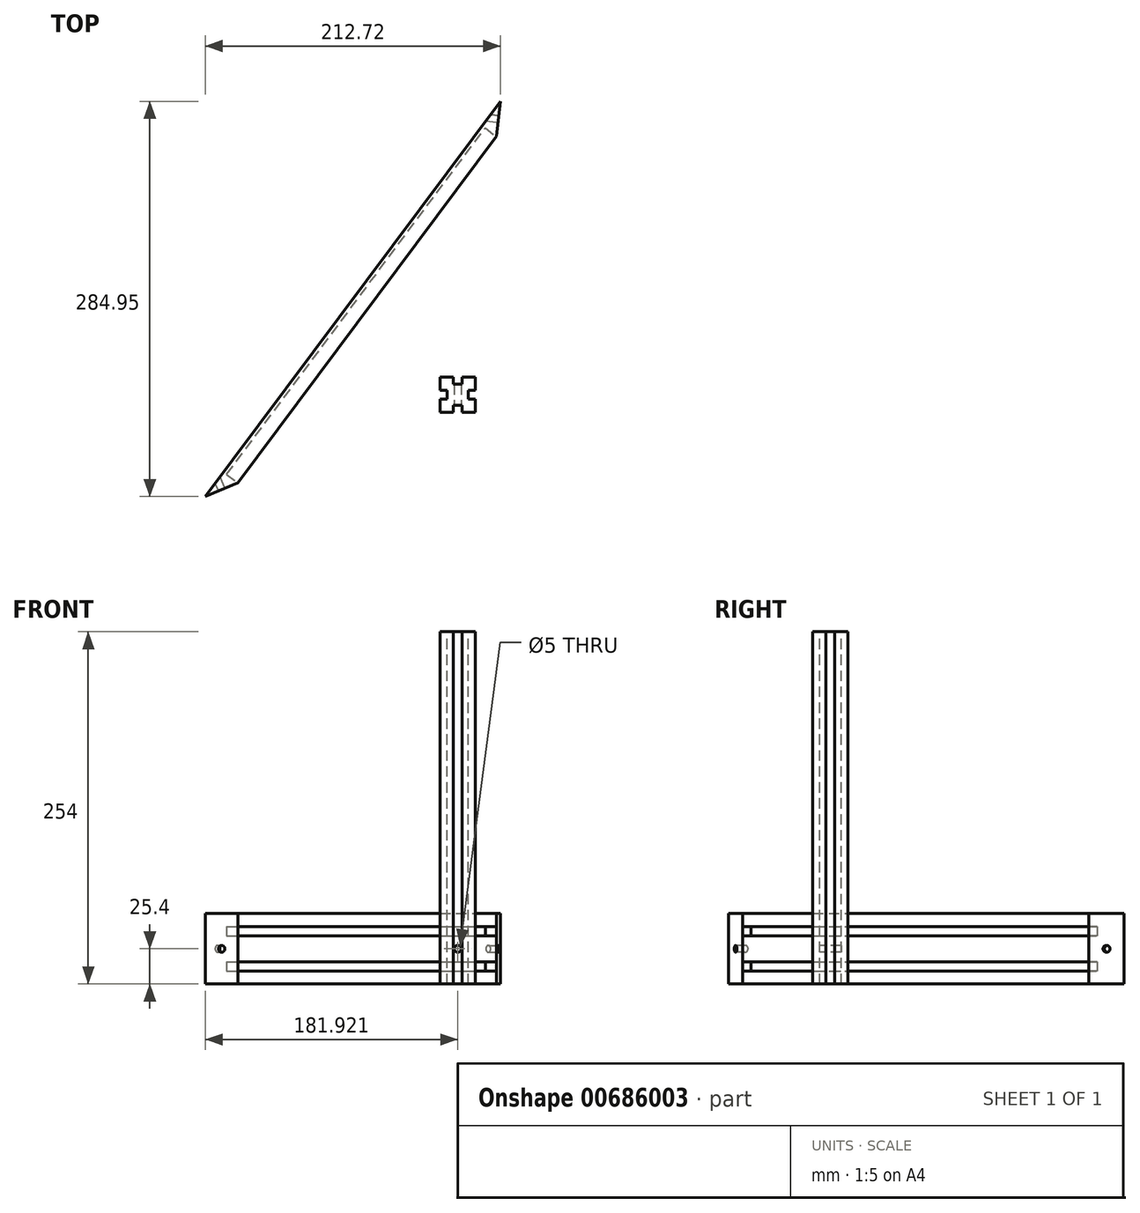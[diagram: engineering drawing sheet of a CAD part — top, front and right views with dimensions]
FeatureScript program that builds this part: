
annotation { "Feature Type Name" : "Feature", "Feature Type Description" : "" }
export const myFeature = defineFeature(function(context is Context, id is Id, definition is map)
    precondition{}
    {
        {
            var Q0;
            Q0=qCreatedBy(makeId("Top.planeOp"),FACE);
            var sketch = newSketch(context, id + "F0", { "sketchPlane" : qUnion([Q0])});
            skLineSegment(sketch, "E0", {"start": v(68.9, 164.34) * mm, "end": v(-143.82, -120.61) * mm});
            skLineSegment(sketch, "E1", {"start": v(-120.49, -110.58) * mm, "end": v(65.92, 139.12) * mm});
            skLineSegment(sketch, "E2", {"start": v(68.9, 164.34) * mm, "end": v(65.92, 139.12) * mm});
            skLineSegment(sketch, "E3", {"start": v(-143.82, -120.61) * mm, "end": v(-120.49, -110.58) * mm});
            skSolve(sketch);
        }
        {
            var Q0;
            Q0=makeQuery(id+"F0.imprint","IMPRINT",FACE,{"disambiguationData":[TD([[makeQuery(id+"F0.imprint","IMPRINT",EDGE,{"derivedFrom":sQuery(id+"F0.wireOp",EDGE,"E0")}),1.0]])]});
            extrude(context, id + "F1", {"entities" : qUnion([Q0]), "depth" : 50.8 * mm, "offsetDistance" : 25 * mm});
        }
        {
            var Q0;
            Q0=makeQuery(id+"F1.opExtrude","SWEPT_FACE",FACE,{"disambiguationData":[OSD([sQuery(id+"F0.wireOp",EDGE,"E1")])]});
            var sketch = newSketch(context, id + "F2", { "sketchPlane" : qUnion([Q0])});
            skLineSegment(sketch, "E4.bottom", {"start": v(-160.69, 15.95) * mm, "end": v(150.92, 15.95) * mm});
            skLineSegment(sketch, "E4.top", {"start": v(-160.69, 9.45) * mm, "end": v(150.92, 9.45) * mm});
            skLineSegment(sketch, "E4.left", {"start": v(-160.69, 15.95) * mm, "end": v(-160.69, 9.45) * mm});
            skLineSegment(sketch, "E4.right", {"start": v(150.92, 15.95) * mm, "end": v(150.92, 9.45) * mm});
            skLineSegment(sketch, "E5.bottom", {"start": v(-160.69, 41.35) * mm, "end": v(150.92, 41.35) * mm});
            skLineSegment(sketch, "E5.top", {"start": v(-160.69, 34.85) * mm, "end": v(150.92, 34.85) * mm});
            skLineSegment(sketch, "E5.left", {"start": v(-160.69, 41.35) * mm, "end": v(-160.69, 34.85) * mm});
            skLineSegment(sketch, "E5.right", {"start": v(150.92, 41.35) * mm, "end": v(150.92, 34.85) * mm});
            skSolve(sketch);
        }
        {
            var Q0;
            Q0=makeQuery(id+"F2.imprint","IMPRINT",FACE,{"disambiguationData":[TD([[makeQuery(id+"F2.imprint","IMPRINT",EDGE,{"derivedFrom":sQuery(id+"F2.wireOp",EDGE,"E5.bottom")}),-1.0]])]});
            var Q1;
            Q1=makeQuery(id+"F2.imprint","IMPRINT",FACE,{"disambiguationData":[TD([[makeQuery(id+"F2.imprint","IMPRINT",EDGE,{"derivedFrom":sQuery(id+"F2.wireOp",EDGE,"E4.bottom")}),-1.0]])]});
            extrude(context, id + "F3", {"entities" : qUnion([Q0, Q1]), "operationType" : NewBodyOperationType.REMOVE, "oppositeDirection" : true, "depth" : 10 * mm, "offsetDistance" : 25 * mm});
        }
        {
            var Q0;
            Q0=qCreatedBy(makeId("Top.planeOp"),FACE);
            var sketch = newSketch(context, id + "F4", { "sketchPlane" : qUnion([Q0])});
            skLineSegment(sketch, "E6.bottom", {"start": v(25.4, -34.55) * mm, "end": v(50.8, -34.55) * mm});
            skLineSegment(sketch, "E6.top", {"start": v(25.4, -59.95) * mm, "end": v(50.8, -59.95) * mm});
            skLineSegment(sketch, "E6.left", {"start": v(25.4, -34.55) * mm, "end": v(25.4, -59.95) * mm});
            skLineSegment(sketch, "E6.right", {"start": v(50.8, -34.55) * mm, "end": v(50.8, -59.95) * mm});
            skSolve(sketch);
        }
        {
            var Q0;
            Q0=makeQuery(id+"F4.imprint","IMPRINT",FACE,{"disambiguationData":[TD([[makeQuery(id+"F4.imprint","IMPRINT",EDGE,{"derivedFrom":sQuery(id+"F4.wireOp",EDGE,"E6.bottom")}),-1.0]])]});
            extrude(context, id + "F5", {"entities" : qUnion([Q0]), "depth" : 254 * mm, "offsetDistance" : 25 * mm});
        }
        {
            var Q0;
            Q0=makeQuery(id+"F5.opExtrude","SWEPT_FACE",FACE,{"disambiguationData":[OSD([sQuery(id+"F4.wireOp",EDGE,"E6.top")])]});
            var sketch = newSketch(context, id + "F6", { "sketchPlane" : qUnion([Q0])});
            skLineSegment(sketch, "E7.bottom", {"start": v(41.35, 0) * mm, "end": v(34.85, 0) * mm});
            skLineSegment(sketch, "E7.top", {"start": v(41.35, 508) * mm, "end": v(34.85, 508) * mm});
            skLineSegment(sketch, "E7.left", {"start": v(41.35, 0) * mm, "end": v(41.35, 508) * mm});
            skLineSegment(sketch, "E7.right", {"start": v(34.85, 0) * mm, "end": v(34.85, 508) * mm});
            skPoint(sketch, "E7.middle", {"position": v(38.1, 254) * mm});
            skSolve(sketch);
        }
        {
            var Q0;
            Q0=makeQuery(id+"F5.opExtrude","SWEPT_FACE",FACE,{"disambiguationData":[OSD([sQuery(id+"F4.wireOp",EDGE,"E6.right")])]});
            var sketch = newSketch(context, id + "F7", { "sketchPlane" : qUnion([Q0])});
            skLineSegment(sketch, "E8.bottom", {"start": v(-44, 0) * mm, "end": v(-50.5, 0) * mm});
            skLineSegment(sketch, "E8.top", {"start": v(-44, 508) * mm, "end": v(-50.5, 508) * mm});
            skLineSegment(sketch, "E8.left", {"start": v(-44, 0) * mm, "end": v(-44, 508) * mm});
            skLineSegment(sketch, "E8.right", {"start": v(-50.5, 0) * mm, "end": v(-50.5, 508) * mm});
            skPoint(sketch, "E8.middle", {"position": v(-47.25, 254) * mm});
            skSolve(sketch);
        }
        {
            var Q0;
            Q0=makeQuery(id+"F5.opExtrude","SWEPT_FACE",FACE,{"disambiguationData":[OSD([sQuery(id+"F4.wireOp",EDGE,"E6.left")])]});
            var sketch = newSketch(context, id + "F8", { "sketchPlane" : qUnion([Q0])});
            skLineSegment(sketch, "E9.bottom", {"start": v(50.5, 0) * mm, "end": v(44, 0) * mm});
            skLineSegment(sketch, "E9.top", {"start": v(50.5, 508) * mm, "end": v(44, 508) * mm});
            skLineSegment(sketch, "E9.left", {"start": v(50.5, 0) * mm, "end": v(50.5, 508) * mm});
            skLineSegment(sketch, "E9.right", {"start": v(44, 0) * mm, "end": v(44, 508) * mm});
            skPoint(sketch, "E9.middle", {"position": v(47.25, 254) * mm});
            skSolve(sketch);
        }
        {
            var Q0;
            Q0=makeQuery(id+"F5.opExtrude","SWEPT_FACE",FACE,{"disambiguationData":[OSD([sQuery(id+"F4.wireOp",EDGE,"E6.bottom")])]});
            var sketch = newSketch(context, id + "F9", { "sketchPlane" : qUnion([Q0])});
            skLineSegment(sketch, "E10.bottom", {"start": v(-34.85, 0) * mm, "end": v(-38.73, 0) * mm});
            skLineSegment(sketch, "E10.top", {"start": v(-32.23, 508) * mm, "end": v(-38.73, 508) * mm});
            skLineSegment(sketch, "E11.bottom", {"start": v(-34.85, 0) * mm, "end": v(-41.35, 0) * mm});
            skLineSegment(sketch, "E11.top", {"start": v(-34.85, 508) * mm, "end": v(-41.35, 508) * mm});
            skLineSegment(sketch, "E11.left", {"start": v(-34.85, 0) * mm, "end": v(-34.85, 508) * mm});
            skLineSegment(sketch, "E11.right", {"start": v(-41.35, 0) * mm, "end": v(-41.35, 508) * mm});
            skPoint(sketch, "E11.middle", {"position": v(-38.1, 254) * mm});
            skSolve(sketch);
        }
        {
            var Q0;
            {var subQ0=sQuery(id+"F7.wireOp",EDGE,"E8.bottom");Q0=makeQuery(id+"F7.imprint","IMPRINT",FACE,{"disambiguationData":[TD([[makeQuery(id+"F7.imprint","IMPRINT",EDGE,{"derivedFrom":subQ0}),-1.0]])]});}
            extrude(context, id + "F10", {"entities" : qUnion([Q0]), "operationType" : NewBodyOperationType.REMOVE, "oppositeDirection" : true, "depth" : 5 * mm, "offsetDistance" : 25 * mm});
        }
        {
            var Q0;
            {var subQ0=sQuery(id+"F9.wireOp",EDGE,"E10.bottom");Q0=makeQuery(id+"F9.imprint","IMPRINT",FACE,{"disambiguationData":[TD([[makeQuery(id+"F9.imprint","IMPRINT",EDGE,{"derivedFrom":subQ0}),-1.0]])]});}
            var Q1;
            {var subQ0=sQuery(id+"F9.wireOp",EDGE,"E11.left");var subQ2=sQuery(id+"F4.wireOp",EDGE,"E6.bottom");var subQ7=makeQuery(id+"F5.opExtrude","CAP_EDGE",EDGE,{"disambiguationData":[OSD([subQ2])],"isStart":false});var subQ8=makeQuery(id+"F9.imprint","INTERSECT",VERTEX,{"derivedFrom":[subQ7,subQ0]});Q1=makeQuery(id+"F9.imprint","IMPRINT",FACE,{"disambiguationData":[TD([[makeQuery(id+"F9.imprint","IMPRINT",EDGE,{"disambiguationData":[TD([[subQ8,-1.0]])],"derivedFrom":subQ7}),1.0]])]});}
            extrude(context, id + "F11", {"entities" : qUnion([Q0, Q1]), "operationType" : NewBodyOperationType.REMOVE, "oppositeDirection" : true, "depth" : 5 * mm, "offsetDistance" : 25 * mm});
        }
        {
            var Q0;
            {var subQ0=sQuery(id+"F8.wireOp",EDGE,"E9.bottom");Q0=makeQuery(id+"F8.imprint","IMPRINT",FACE,{"disambiguationData":[TD([[makeQuery(id+"F8.imprint","IMPRINT",EDGE,{"derivedFrom":subQ0}),1.0]])]});}
            extrude(context, id + "F12", {"entities" : qUnion([Q0]), "operationType" : NewBodyOperationType.REMOVE, "oppositeDirection" : true, "depth" : 5 * mm, "offsetDistance" : 25 * mm});
        }
        {
            var Q0;
            {var subQ0=sQuery(id+"F6.wireOp",EDGE,"E7.bottom");Q0=makeQuery(id+"F6.imprint","IMPRINT",FACE,{"disambiguationData":[TD([[makeQuery(id+"F6.imprint","IMPRINT",EDGE,{"derivedFrom":subQ0}),1.0]])]});}
            extrude(context, id + "F13", {"entities" : qUnion([Q0]), "operationType" : NewBodyOperationType.REMOVE, "oppositeDirection" : true, "depth" : 5 * mm, "offsetDistance" : 25 * mm});
        }
        {
            var Q0;
            Q0=makeQuery(id+"F1.opExtrude","SWEPT_FACE",FACE,{"disambiguationData":[OSD([sQuery(id+"F0.wireOp",EDGE,"E2")])]});
            var sketch = newSketch(context, id + "F14", { "sketchPlane" : qUnion([Q0])});
            skCircle(sketch, "E12", {"center": v(158.6, 25.4) * mm, "radius": 2.5 * mm});
            skSolve(sketch);
        }
        {
            var Q0;
            Q0=makeQuery(id+"F14.imprint","IMPRINT",FACE,{"disambiguationData":[TD([[makeQuery(id+"F14.imprint","IMPRINT",EDGE,{"derivedFrom":sQuery(id+"F14.wireOp",EDGE,"E12")}),1.0]])]});
            extrude(context, id + "F15", {"entities" : qUnion([Q0]), "operationType" : NewBodyOperationType.REMOVE, "oppositeDirection" : true, "depth" : 100 * mm, "offsetDistance" : 25 * mm});
        }
        {
            var Q0;
            Q0=makeQuery(id+"F1.opExtrude","SWEPT_FACE",FACE,{"disambiguationData":[OSD([sQuery(id+"F0.wireOp",EDGE,"E3")])]});
            var sketch = newSketch(context, id + "F16", { "sketchPlane" : qUnion([Q0])});
            skCircle(sketch, "E13", {"center": v(-167.06, 25.4) * mm, "radius": 2.5 * mm});
            skSolve(sketch);
        }
        {
            var Q0;
            Q0=makeQuery(id+"F16.imprint","IMPRINT",FACE,{"disambiguationData":[TD([[makeQuery(id+"F16.imprint","IMPRINT",EDGE,{"derivedFrom":sQuery(id+"F16.wireOp",EDGE,"E13")}),1.0]])]});
            extrude(context, id + "F17", {"entities" : qUnion([Q0]), "operationType" : NewBodyOperationType.REMOVE, "oppositeDirection" : true, "depth" : 25 * mm, "offsetDistance" : 25 * mm});
        }
        {
            var Q0;
            Q0=makeQuery(id+"F13.boolean.opBoolean","COPY",FACE,{"derivedFrom":makeQuery(id+"F13.opExtrude","CAP_FACE",FACE,{"disambiguationData":[OSD([sQuery(id+"F4.wireOp",EDGE,"E6.top"),sQuery(id+"F6.wireOp",EDGE,"E7.bottom"),sQuery(id+"F6.wireOp",EDGE,"E7.left"),sQuery(id+"F6.wireOp",EDGE,"E7.right")])],"isStart":false})});
            var sketch = newSketch(context, id + "F18", { "sketchPlane" : qUnion([Q0])});
            skCircle(sketch, "E14", {"center": v(38.1, 25.4) * mm, "radius": 2.5 * mm});
            skSolve(sketch);
        }
        {
            var Q0;
            Q0 = qSketchRegion(id + "F18", true);
            extrude(context, id + "F19", {"entities" : qUnion([Q0]), "operationType" : NewBodyOperationType.REMOVE, "oppositeDirection" : true, "depth" : 25 * mm, "offsetDistance" : 25 * mm});
        }
    });
